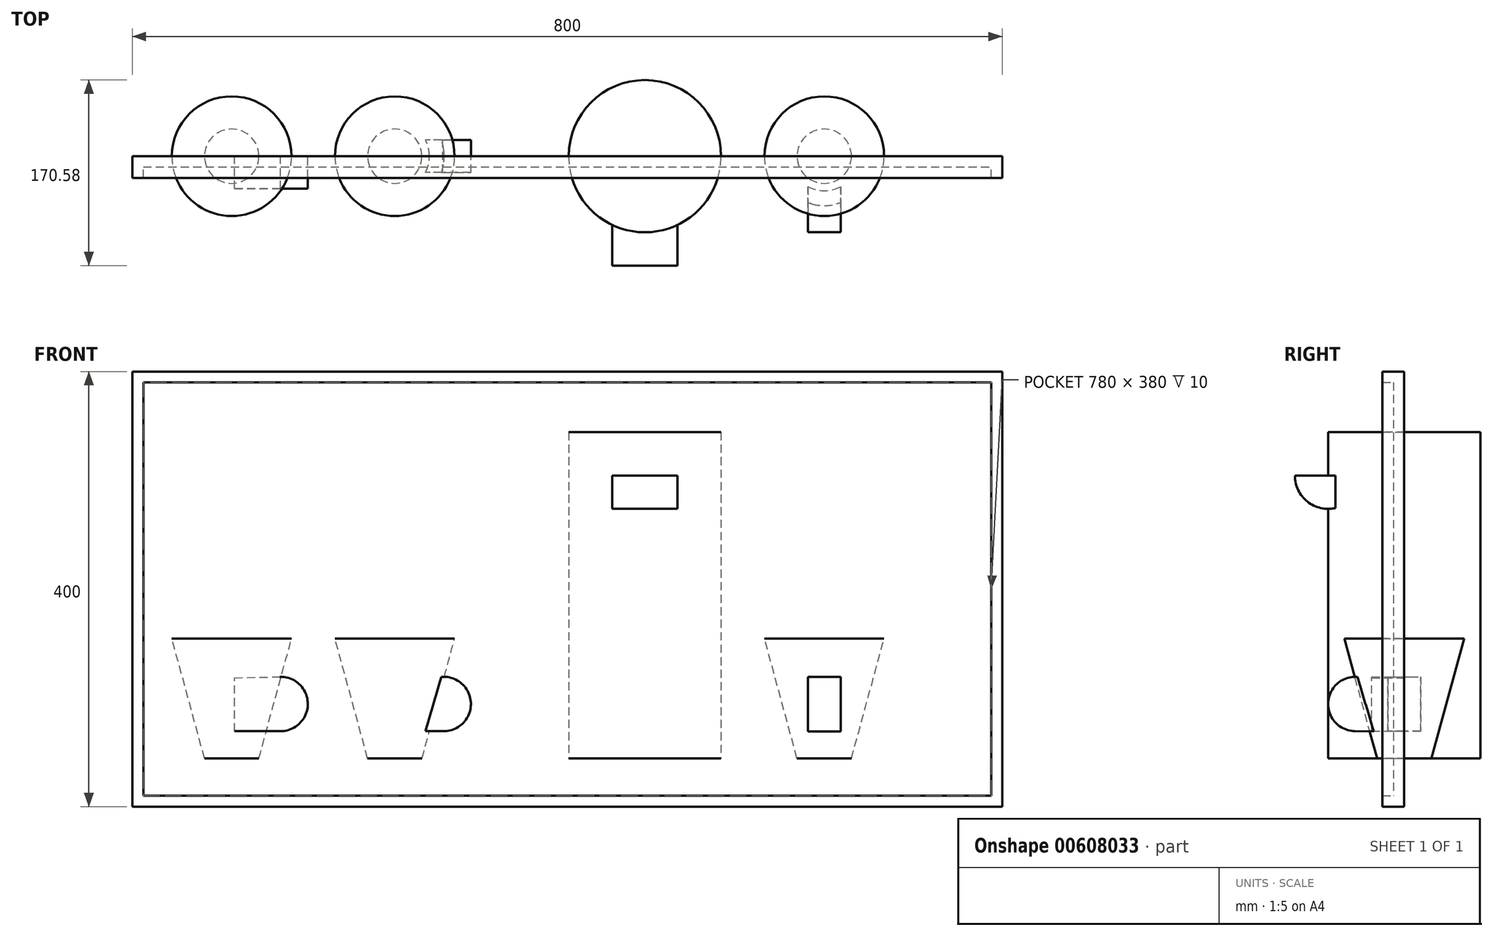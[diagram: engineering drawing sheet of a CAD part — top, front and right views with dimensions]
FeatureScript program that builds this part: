
annotation { "Feature Type Name" : "Feature", "Feature Type Description" : "" }
export const myFeature = defineFeature(function(context is Context, id is Id, definition is map)
    precondition{}
    {
        {
            var Q0;
            Q0=qCreatedBy(makeId("Top.planeOp"),FACE);
            cPlane(context, id + "F0", {"entities" : qUnion([Q0]), "cplaneType" : CPlaneType.OFFSET, "offset" : 110 * mm, "width" : 150 * mm, "height" : 150 * mm});
        }
        {
            var Q0;
            Q0=qCreatedBy(makeId("Top.planeOp"),FACE);
            var sketch = newSketch(context, id + "F1", { "sketchPlane" : qUnion([Q0])});
            skCircle(sketch, "E0", {"center": v(70, 0) * mm, "radius": 70 * mm});
            skSolve(sketch);
        }
        {
            var Q0;
            Q0=qSketchRegion(id+"F1",true);
            var Q1;
            Q1=qSketchRegion(id+"F3",true);
            extrude(context, id + "F2", {"entities" : qUnion([Q0, Q1]), "depth" : 300 * mm, "offsetDistance" : 25 * mm});
        }
        {
            var Q0;
            Q0=qCreatedBy(makeId("Top.planeOp"),FACE);
            var sketch = newSketch(context, id + "F3", { "sketchPlane" : qUnion([Q0])});
            skCircle(sketch, "E1", {"center": v(235, 0) * mm, "radius": 25 * mm});
            skSolve(sketch);
        }
        {
            var Q0;
            Q0=qCreatedBy(id+"F0.planeOp",FACE);
            var sketch = newSketch(context, id + "F4", { "sketchPlane" : qUnion([Q0])});
            skCircle(sketch, "E2", {"center": v(235, 0) * mm, "radius": 55 * mm});
            skSolve(sketch);
        }
        {
            var Q0;
            Q0=qSketchRegion(id+"F3",true);
            var Q1;
            Q1=qSketchRegion(id+"F4",true);
            loft(context, id + "F5", {"sheetProfilesArray" : [{ "sheetProfileEntities" : qUnion([Q0]) }, { "sheetProfileEntities" : qUnion([Q1]) }]});
        }
        {
            var Q0;
            Q0=qCreatedBy(makeId("Top.planeOp"),FACE);
            var sketch = newSketch(context, id + "F6", { "sketchPlane" : qUnion([Q0])});
            skCircle(sketch, "E3", {"center": v(-160, 0) * mm, "radius": 25 * mm});
            skSolve(sketch);
        }
        {
            var Q0;
            Q0=qCreatedBy(id+"F0.planeOp",FACE);
            var sketch = newSketch(context, id + "F7", { "sketchPlane" : qUnion([Q0])});
            skCircle(sketch, "E4", {"center": v(-160, 0) * mm, "radius": 55 * mm});
            skSolve(sketch);
        }
        {
            var Q0;
            Q0=qSketchRegion(id+"F6",true);
            var Q1;
            Q1=qSketchRegion(id+"F7",true);
            loft(context, id + "F8", {"sheetProfilesArray" : [{ "sheetProfileEntities" : qUnion([Q0]) }, { "sheetProfileEntities" : qUnion([Q1]) }]});
        }
        {
            var Q0;
            Q0=qCreatedBy(makeId("Top.planeOp"),FACE);
            var sketch = newSketch(context, id + "F9", { "sketchPlane" : qUnion([Q0])});
            skCircle(sketch, "E5", {"center": v(-310, 0) * mm, "radius": 25 * mm});
            skSolve(sketch);
        }
        {
            var Q0;
            Q0=qCreatedBy(id+"F0.planeOp",FACE);
            var sketch = newSketch(context, id + "F10", { "sketchPlane" : qUnion([Q0])});
            skCircle(sketch, "E6", {"center": v(-310, 0) * mm, "radius": 55 * mm});
            skSolve(sketch);
        }
        {
            var Q0;
            Q0=qSketchRegion(id+"F9",true);
            var Q1;
            Q1=qSketchRegion(id+"F10",true);
            loft(context, id + "F11", {"sheetProfilesArray" : [{ "sheetProfileEntities" : qUnion([Q0]) }, { "sheetProfileEntities" : qUnion([Q1]) }]});
        }
        {
            var Q0;
            Q0=qCreatedBy(makeId("Right.planeOp"),FACE);
            cPlane(context, id + "F12", {"entities" : qUnion([Q0]), "cplaneType" : CPlaneType.OFFSET, "offset" : 70 * mm, "width" : 150 * mm, "height" : 150 * mm});
        }
        {
            var Q0;
            Q0=qCreatedBy(id+"F12.planeOp",FACE);
            var sketch = newSketch(context, id + "F13", { "sketchPlane" : qUnion([Q0])});
            skArc(sketch, "E7", {"start": v(-100.58, 259.93) * mm, "mid": v(-70, 229.42) * mm, "end": v(-39.42, 259.93) * mm});
            skLineSegment(sketch, "E8", {"start": v(-39.42, 259.93) * mm, "end": v(-100.58, 259.93) * mm});
            skSolve(sketch);
        }
        {
            var Q0;
            Q0=qSketchRegion(id+"F13",true);
            extrude(context, id + "F14", {"entities" : qUnion([Q0]), "operationType" : NewBodyOperationType.ADD, "endBound" : BoundingType.SYMMETRIC, "depth" : 60 * mm, "offsetDistance" : 25 * mm});
        }
        {
            var Q0;
            Q0=qCreatedBy(makeId("Right.planeOp"),FACE);
            cPlane(context, id + "F15", {"entities" : qUnion([Q0]), "cplaneType" : CPlaneType.OFFSET, "offset" : 235 * mm, "width" : 150 * mm, "height" : 150 * mm});
        }
        {
            var Q0;
            Q0=qCreatedBy(id+"F15.planeOp",FACE);
            var sketch = newSketch(context, id + "F16", { "sketchPlane" : qUnion([Q0])});
            skArc(sketch, "E9", {"start": v(-44.02, 74.98) * mm, "mid": v(-69.99, 50.74) * mm, "end": v(-45.51, 25) * mm});
            skLineSegment(sketch, "E10", {"start": v(-45.51, 25) * mm, "end": v(-13.64, 24.35) * mm});
            skLineSegment(sketch, "E11", {"start": v(-13.64, 24.35) * mm, "end": v(-13.64, 73.8) * mm});
            skLineSegment(sketch, "E12", {"start": v(-13.64, 73.8) * mm, "end": v(-44.02, 74.98) * mm});
            skSolve(sketch);
        }
        {
            var Q0;
            Q0=qSketchRegion(id+"F16",true);
            extrude(context, id + "F17", {"entities" : qUnion([Q0]), "operationType" : NewBodyOperationType.ADD, "endBound" : BoundingType.SYMMETRIC, "depth" : 30 * mm, "offsetDistance" : 25 * mm});
        }
        {
            var Q0;
            Q0=qCreatedBy(makeId("Front.planeOp"),FACE);
            var sketch = newSketch(context, id + "F18", { "sketchPlane" : qUnion([Q0])});
            skArc(sketch, "E13", {"start": v(-115.89, 25.02) * mm, "mid": v(-90, 49.5) * mm, "end": v(-114.88, 75) * mm});
            skLineSegment(sketch, "E14", {"start": v(-115.89, 25.02) * mm, "end": v(-153.4, 25.02) * mm});
            skLineSegment(sketch, "E15", {"start": v(-153.4, 25.02) * mm, "end": v(-153.4, 75.18) * mm});
            skLineSegment(sketch, "E16", {"start": v(-153.4, 75.18) * mm, "end": v(-114.88, 75) * mm});
            skSolve(sketch);
        }
        {
            var Q0;
            Q0=qSketchRegion(id+"F18",true);
            extrude(context, id + "F19", {"entities" : qUnion([Q0]), "operationType" : NewBodyOperationType.ADD, "endBound" : BoundingType.SYMMETRIC, "depth" : 30 * mm, "offsetDistance" : 25 * mm});
        }
        {
            var Q0;
            Q0=qCreatedBy(makeId("Front.planeOp"),FACE);
            var sketch = newSketch(context, id + "F20", { "sketchPlane" : qUnion([Q0])});
            skArc(sketch, "E17", {"start": v(-265.26, 25) * mm, "mid": v(-240, 50.18) * mm, "end": v(-265.62, 75) * mm});
            skLineSegment(sketch, "E18", {"start": v(-264.74, 25) * mm, "end": v(-307.4, 25) * mm});
            skLineSegment(sketch, "E19", {"start": v(-307.4, 25) * mm, "end": v(-307.4, 73.96) * mm});
            skLineSegment(sketch, "E20", {"start": v(-307.4, 73.96) * mm, "end": v(-265.62, 75) * mm});
            skSolve(sketch);
        }
        {
            var Q0;
            Q0 = qSketchRegion(id + "F20", true);
            extrude(context, id + "F21", {"entities" : qUnion([Q0]), "depth" : 30 * mm, "offsetDistance" : 25 * mm});
        }
        {
            var Q0;
            Q0=qCreatedBy(makeId("Front.planeOp"),FACE);
            var sketch = newSketch(context, id + "F22", { "sketchPlane" : qUnion([Q0])});
            skLineSegment(sketch, "E21.bottom", {"start": v(-401.33, 355.64) * mm, "end": v(398.67, 355.64) * mm});
            skLineSegment(sketch, "E21.top", {"start": v(-401.33, -44.36) * mm, "end": v(398.67, -44.36) * mm});
            skLineSegment(sketch, "E21.left", {"start": v(-401.33, 355.64) * mm, "end": v(-401.33, -44.36) * mm});
            skLineSegment(sketch, "E21.right", {"start": v(398.67, 355.64) * mm, "end": v(398.67, -44.36) * mm});
            skSolve(sketch);
        }
        {
            var Q0;
            Q0=qCreatedBy(makeId("Front.planeOp"),FACE);
            cPlane(context, id + "F23", {"entities" : qUnion([Q0]), "cplaneType" : CPlaneType.OFFSET, "offset" : 30 * mm, "oppositeDirection" : true, "width" : 150 * mm, "height" : 150 * mm});
        }
        {
            var Q0;
            Q0 = qSketchRegion(id + "F22", true);
            extrude(context, id + "F24", {"entities" : qUnion([Q0]), "depth" : 20 * mm, "offsetDistance" : 25 * mm});
        }
        {
            var Q0;
            Q0=makeQuery(id+"F24.opExtrude","CAP_FACE",FACE,{"disambiguationData":[OSD([sQuery(id+"F22.wireOp",EDGE,"E21.bottom"),sQuery(id+"F22.wireOp",EDGE,"E21.top"),sQuery(id+"F22.wireOp",EDGE,"E21.left"),sQuery(id+"F22.wireOp",EDGE,"E21.right")])],"isStart":false});
            shell(context, id + "F25", {"entities" : qUnion([Q0]), "thickness" : 10 * mm});
        }
    });
